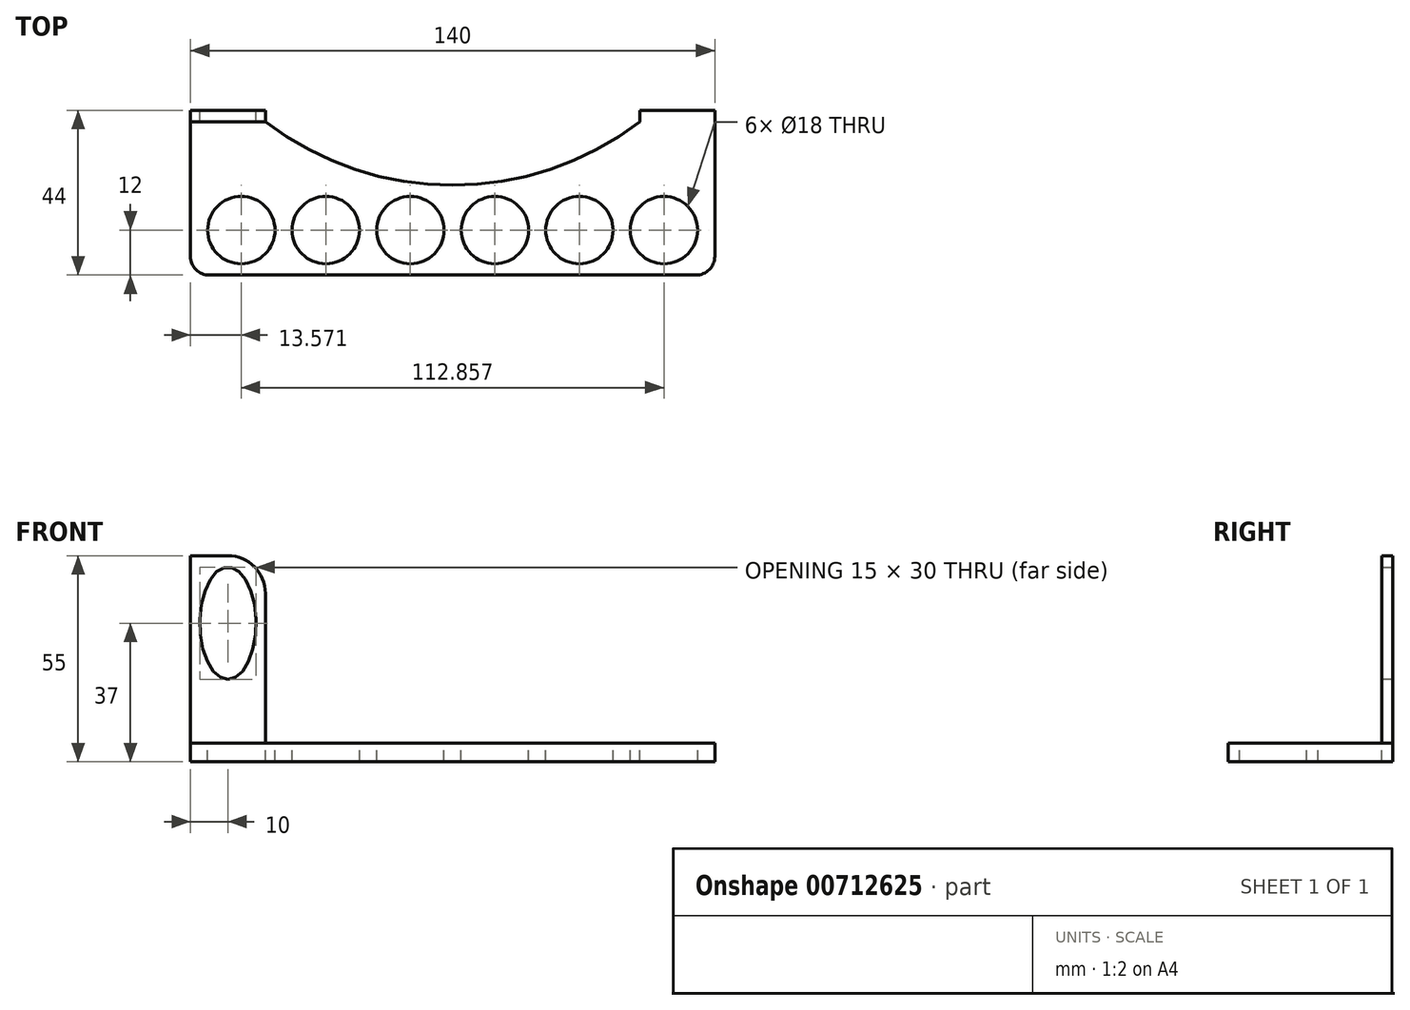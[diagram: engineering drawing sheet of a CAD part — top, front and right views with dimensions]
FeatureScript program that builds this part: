
annotation { "Feature Type Name" : "Feature", "Feature Type Description" : "" }
export const myFeature = defineFeature(function(context is Context, id is Id, definition is map)
    precondition{}
    {
        {
            var Q0;
            Q0=qCreatedBy(makeId("Top.planeOp"),FACE);
            var sketch = newSketch(context, id + "F0", { "sketchPlane" : qUnion([Q0])});
            skLineSegment(sketch, "E0.bottom", {"start": v(70, -20) * mm, "end": v(-70, -20) * mm, "construction": true});
            skLineSegment(sketch, "E0.top", {"start": v(70, 20) * mm, "end": v(-70, 20) * mm, "construction": true});
            skLineSegment(sketch, "E0.left", {"start": v(70, -20) * mm, "end": v(70, 20) * mm, "construction": true});
            skLineSegment(sketch, "E0.right", {"start": v(-70, -20) * mm, "end": v(-70, 20) * mm, "construction": true});
            skPoint(sketch, "E0.middle", {"position": v(0, 0) * mm});
            skLineSegment(sketch, "E1.bottom", {"start": v(-70, -20) * mm, "end": v(70, -20) * mm});
            skLineSegment(sketch, "E1.top", {"start": v(-65, -44) * mm, "end": v(65, -44) * mm});
            skLineSegment(sketch, "E1.left", {"start": v(-70, -20) * mm, "end": v(-70, -39) * mm});
            skLineSegment(sketch, "E1.right", {"start": v(70, -20) * mm, "end": v(70, -39) * mm});
            skLineSegment(sketch, "E2", {"start": v(-70, -41) * mm, "end": v(70, -41) * mm, "construction": true});
            skCircle(sketch, "E3", {"center": v(-56.43, -32) * mm, "radius": 9 * mm});
            skCircle(sketch, "E4", {"center": v(-33.86, -32) * mm, "radius": 9 * mm});
            skCircle(sketch, "E5", {"center": v(-11.29, -32) * mm, "radius": 9 * mm});
            skCircle(sketch, "E6", {"center": v(11.29, -32) * mm, "radius": 9 * mm});
            skCircle(sketch, "E7", {"center": v(33.86, -32) * mm, "radius": 9 * mm});
            skCircle(sketch, "E8", {"center": v(56.43, -32) * mm, "radius": 9 * mm});
            skLineSegment(sketch, "E9", {"start": v(56.43, -32) * mm, "end": v(65.43, -32) * mm, "construction": true});
            skLineSegment(sketch, "E10", {"start": v(65.43, -32) * mm, "end": v(70, -32) * mm, "construction": true});
            skLineSegment(sketch, "E11", {"start": v(56.43, -32) * mm, "end": v(47.43, -32) * mm, "construction": true});
            skLineSegment(sketch, "E12", {"start": v(47.43, -32) * mm, "end": v(42.86, -32) * mm, "construction": true});
            skLineSegment(sketch, "E13", {"start": v(42.86, -32) * mm, "end": v(24.86, -32) * mm, "construction": true});
            skLineSegment(sketch, "E14", {"start": v(24.86, -32) * mm, "end": v(20.29, -32) * mm, "construction": true});
            skLineSegment(sketch, "E15", {"start": v(20.29, -32) * mm, "end": v(11.29, -32) * mm, "construction": true});
            skLineSegment(sketch, "E16", {"start": v(2.29, -32) * mm, "end": v(-2.29, -32) * mm, "construction": true});
            skLineSegment(sketch, "E17", {"start": v(-2.29, -32) * mm, "end": v(-20.29, -32) * mm, "construction": true});
            skLineSegment(sketch, "E18", {"start": v(-20.29, -32) * mm, "end": v(-24.86, -32) * mm, "construction": true});
            skLineSegment(sketch, "E19", {"start": v(-24.86, -32) * mm, "end": v(-42.86, -32) * mm, "construction": true});
            skLineSegment(sketch, "E20", {"start": v(-42.86, -32) * mm, "end": v(-47.43, -32) * mm, "construction": true});
            skLineSegment(sketch, "E21", {"start": v(-47.43, -32) * mm, "end": v(-65.43, -32) * mm, "construction": true});
            skLineSegment(sketch, "E22", {"start": v(-65.43, -32) * mm, "end": v(-70, -32) * mm, "construction": true});
            skLineSegment(sketch, "E23", {"start": v(-70, 0) * mm, "end": v(-70, -20) * mm});
            skLineSegment(sketch, "E24", {"start": v(70, 0) * mm, "end": v(70, -20) * mm});
            skPoint(sketch, "E25.visualSharp", {"position": v(-70, -44) * mm});
            skArc(sketch, "E25.filletArc", {"start": v(-70, -39) * mm, "mid": v(-68.54, -42.54) * mm, "end": v(-65, -44) * mm});
            skPoint(sketch, "E26.visualSharp", {"position": v(70, -44) * mm});
            skArc(sketch, "E26.filletArc", {"start": v(65, -44) * mm, "mid": v(68.54, -42.54) * mm, "end": v(70, -39) * mm});
            skArc(sketch, "E27", {"start": v(-50, -3) * mm, "mid": v(0, -20) * mm, "end": v(50, -3) * mm});
            skLineSegment(sketch, "E28.bottom", {"start": v(-70, 0) * mm, "end": v(70, 0) * mm, "construction": true});
            skLineSegment(sketch, "E28.top", {"start": v(-70, -3) * mm, "end": v(70, -3) * mm, "construction": true});
            skLineSegment(sketch, "E28.left", {"start": v(-70, 0) * mm, "end": v(-70, -3) * mm, "construction": true});
            skLineSegment(sketch, "E28.right", {"start": v(70, 0) * mm, "end": v(70, -3) * mm, "construction": true});
            skLineSegment(sketch, "E29", {"start": v(50, -3) * mm, "end": v(70, -3) * mm});
            skLineSegment(sketch, "E30.top", {"start": v(-70, -3) * mm, "end": v(-50, -3) * mm});
            skLineSegment(sketch, "E31", {"start": v(-50, -3) * mm, "end": v(50, -3) * mm, "construction": true});
            skLineSegment(sketch, "E32.bottom", {"start": v(-70, 0) * mm, "end": v(-50, 0) * mm});
            skLineSegment(sketch, "E32.left", {"start": v(-70, 0) * mm, "end": v(-70, -3) * mm});
            skLineSegment(sketch, "E32.right", {"start": v(-50, 0) * mm, "end": v(-50, -3) * mm});
            skLineSegment(sketch, "E33.bottom", {"start": v(70, -3) * mm, "end": v(50, -3) * mm});
            skLineSegment(sketch, "E33.top", {"start": v(70, 0) * mm, "end": v(50, 0) * mm});
            skLineSegment(sketch, "E33.left", {"start": v(70, -3) * mm, "end": v(70, 0) * mm});
            skLineSegment(sketch, "E33.right", {"start": v(50, -3) * mm, "end": v(50, 0) * mm});
            skSolve(sketch);
        }
        {
            var Q0;
            {var subQ4=sQuery(id+"F0.wireOp",EDGE,"E23");Q0=makeQuery(id+"F0.imprint","IMPRINT",FACE,{"disambiguationData":[TD([[makeQuery(id+"F0.imprint","IMPRINT",EDGE,{"derivedFrom":subQ4}),1.0]])]});}
            var Q1;
            Q1=makeQuery(id+"F0.imprint","IMPRINT",FACE,{"disambiguationData":[TD([[makeQuery(id+"F0.imprint","IMPRINT",EDGE,{"derivedFrom":sQuery(id+"F0.wireOp",EDGE,"E1.top")}),1.0]])]});
            var Q2;
            {var subQ4=sQuery(id+"F0.wireOp",EDGE,"E24");Q2=makeQuery(id+"F0.imprint","IMPRINT",FACE,{"disambiguationData":[TD([[makeQuery(id+"F0.imprint","IMPRINT",EDGE,{"derivedFrom":subQ4}),-1.0]])]});}
            var Q3;
            Q3=makeQuery(id+"F0.imprint","IMPRINT",FACE,{"disambiguationData":[TD([[makeQuery(id+"F0.imprint","IMPRINT",EDGE,{"derivedFrom":sQuery(id+"F0.wireOp",EDGE,"E32.bottom")}),-1.0]])]});
            var Q4;
            Q4=makeQuery(id+"F0.imprint","IMPRINT",FACE,{"disambiguationData":[TD([[makeQuery(id+"F0.imprint","IMPRINT",EDGE,{"derivedFrom":sQuery(id+"F0.wireOp",EDGE,"E33.bottom")}),-1.0]])]});
            extrude(context, id + "F1", {"entities" : qUnion([Q0, Q1, Q2, Q3, Q4]), "oppositeDirection" : true, "depth" : 5 * mm, "offsetDistance" : 25 * mm});
        }
        {
            var Q0;
            Q0=makeQuery(id+"F0.imprint","IMPRINT",FACE,{"disambiguationData":[TD([[makeQuery(id+"F0.imprint","IMPRINT",EDGE,{"derivedFrom":sQuery(id+"F0.wireOp",EDGE,"E32.bottom")}),-1.0]])]});
            var Q1;
            Q1=makeQuery(id+"F0.imprint","IMPRINT",FACE,{"disambiguationData":[TD([[makeQuery(id+"F0.imprint","IMPRINT",EDGE,{"derivedFrom":sQuery(id+"F0.wireOp",EDGE,"E33.bottom")}),-1.0]])]});
            extrude(context, id + "F2", {"entities" : qUnion([Q0, Q1]), "operationType" : NewBodyOperationType.ADD, "depth" : 50 * mm, "offsetDistance" : 25 * mm});
        }
        {
            var Q0;
            Q0=makeQuery(id+"F2.opExtrude","SWEPT_FACE",FACE,{"disambiguationData":[OSD([sQuery(id+"F0.wireOp",EDGE,"E30.top")])]});
            var sketch = newSketch(context, id + "F3", { "sketchPlane" : qUnion([Q0])});
            skEllipse(sketch, "E34", {"center": v(-60, 32) * mm, "majorRadius": 15 * mm, "minorRadius": 7.5 * mm, "majorAxis": v(0, -1)});
            skLineSegment(sketch, "E35", {"start": v(-70, 0) * mm, "end": v(-70, 50) * mm, "construction": true});
            skLineSegment(sketch, "E36", {"start": v(-70, 50) * mm, "end": v(-50, 50) * mm, "construction": true});
            skEllipse(sketch, "E37.MirrorC", {"center": v(60, 32) * mm, "majorRadius": 15 * mm, "minorRadius": 7.5 * mm, "majorAxis": v(0, -1)});
            skSolve(sketch);
        }
        {
            var Q0;
            Q0=makeQuery(id+"F3.imprint","IMPRINT",FACE,{"disambiguationData":[TD([[makeQuery(id+"F3.imprint","IMPRINT",EDGE,{"derivedFrom":sQuery(id+"F3.wireOp",EDGE,"E34")}),1.0]])]});
            var Q1;
            Q1=makeQuery(id+"F3.imprint","IMPRINT",FACE,{"disambiguationData":[TD([[makeQuery(id+"F3.imprint","IMPRINT",EDGE,{"derivedFrom":sQuery(id+"F3.wireOp",EDGE,"E37.MirrorC")}),1.0]])]});
            extrude(context, id + "F4", {"entities" : qUnion([Q0, Q1]), "operationType" : NewBodyOperationType.REMOVE, "endBound" : BoundingType.SYMMETRIC, "oppositeDirection" : true, "depth" : 25 * mm, "offsetDistance" : 25 * mm});
        }
        {
            var Q0;
            Q0=makeQuery(id+"F2.opExtrude","CAP_EDGE",EDGE,{"disambiguationData":[OSD([sQuery(id+"F0.wireOp",EDGE,"E32.left")])],"isStart":false});
            var Q1;
            Q1=makeQuery(id+"F2.opExtrude","CAP_EDGE",EDGE,{"disambiguationData":[OSD([sQuery(id+"F0.wireOp",EDGE,"E32.right")])],"isStart":false});
            var Q2;
            Q2=makeQuery(id+"F2.opExtrude","CAP_EDGE",EDGE,{"disambiguationData":[OSD([sQuery(id+"F0.wireOp",EDGE,"E33.left")])],"isStart":false});
            var Q3;
            Q3=makeQuery(id+"F2.opExtrude","CAP_EDGE",EDGE,{"disambiguationData":[OSD([sQuery(id+"F0.wireOp",EDGE,"E33.right")])],"isStart":false});
            fillet(context, id + "F5", {"entities" : qUnion([Q0, Q1, Q2, Q3]), "radius" : 10 * mm, "tangentPropagation" : true, "allowEdgeOverflow" : false});
        }
    });
